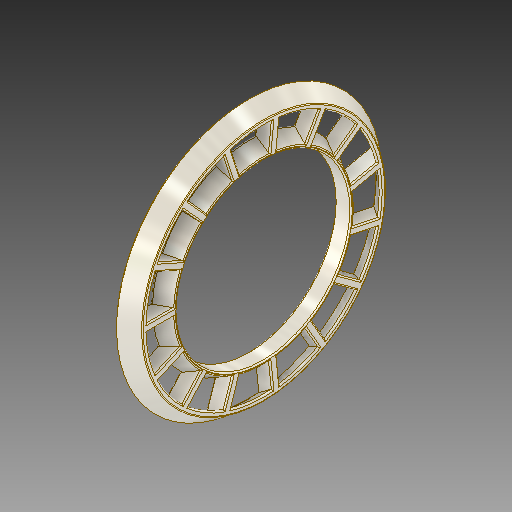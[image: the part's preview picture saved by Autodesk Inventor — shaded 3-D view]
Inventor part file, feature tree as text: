
AUTODESK INVENTOR PART (.ipt)
format: ipt  version: 2019 (Build 230136000, 136)  size: 849,920 bytes
history: native  units: mm
features: sketch x2, revolve x2, split x2, other x2, extrude x1, plane x1, pattern_circular x1, boolean_combine x1, surface_op x1
ambient origin geometry x8: Origin, YZ Plane, XZ Plane, XY Plane, X Axis, Y Axis, Z Axis, Center Point
bodies: Solid3 (feature_tree), Solid2 (feature_tree)
feature tree (13):
  sketch  "Sketch1"  dims[d11=90.0deg d12=90.0deg]
  revolve  "Revolution1"  Angle=90.0deg
  revolve  "Revolution2"  [1 undecoded]
  extrude  "Extrusion1"  TaperAngle=0.0deg  [1 undecoded]
  plane  "Work Plane1"
  split  "Split1"
  split  "Split2"
  pattern_circular  "Circular Pattern1"  Count=15 Angle=360.0deg
  boolean_combine  "Combine1"
  other  "Rule Fillet1"
  sketch  "Sketch2"  dims[d13=6.0mm d14=10.0mm d15=0.0mm d16=0.0mm d17=150.0mm d18=360.0deg d20=1.0mm d22=5.0mm d23=70.5mm d24=37.0mm d25=1.0mm d26=4.0mm d27=9.25mm d28=2.0mm d29=13.0mm d30=9.0mm]
  surface_op  "Surface2"
  other  "Srf2"
note: 2 required parameter values undecoded (feature->parameter linkage not recoverable at this tier; creation-order binding heuristic only, values carry confidence <= 0.55)